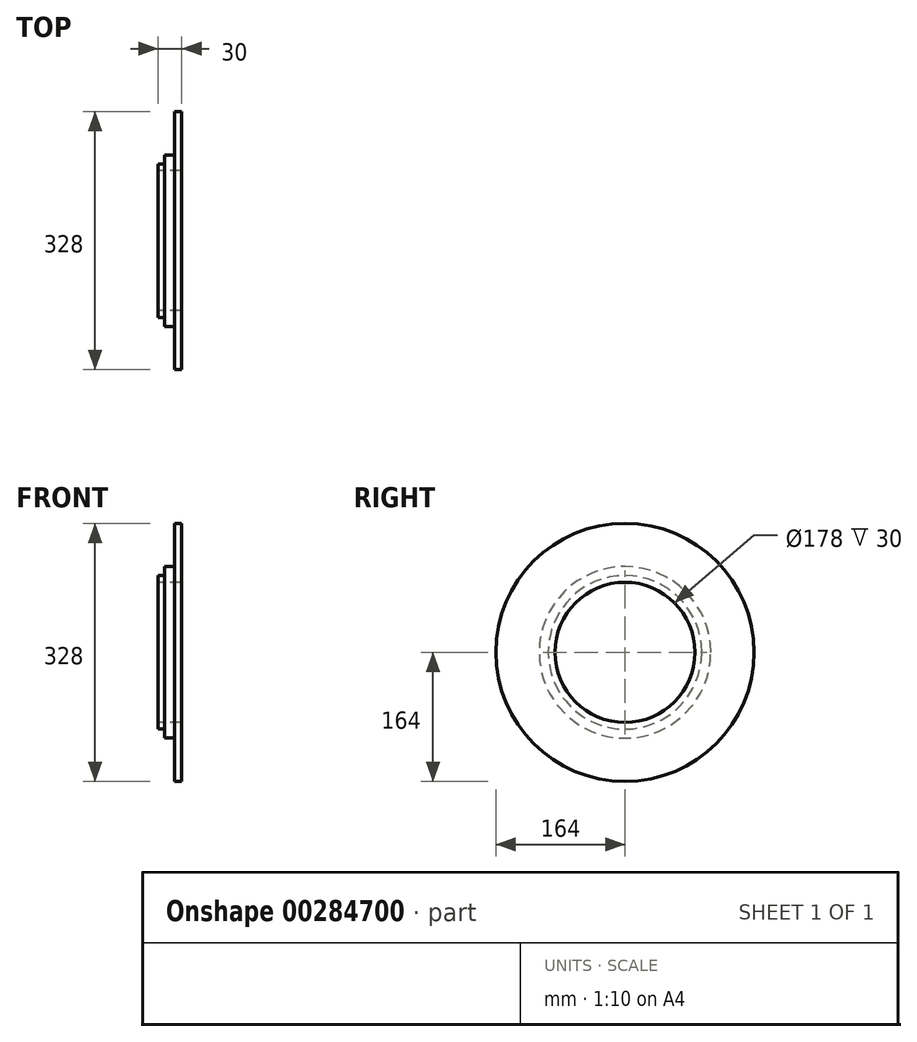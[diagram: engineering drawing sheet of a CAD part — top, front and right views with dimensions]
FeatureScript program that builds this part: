
annotation { "Feature Type Name" : "Feature", "Feature Type Description" : "" }
export const myFeature = defineFeature(function(context is Context, id is Id, definition is map)
    precondition{}
    {
        {
            var Q0;
            Q0=qCreatedBy(makeId("Front.planeOp"),FACE);
            var sketch = newSketch(context, id + "F0", { "sketchPlane" : qUnion([Q0])});
            skLineSegment(sketch, "E0", {"start": v(0, 89) * mm, "end": v(0, 164) * mm});
            skLineSegment(sketch, "E1", {"start": v(0, 164) * mm, "end": v(8, 164) * mm});
            skLineSegment(sketch, "E2", {"start": v(8, 164) * mm, "end": v(8, 89) * mm});
            skLineSegment(sketch, "E3", {"start": v(21, 89) * mm, "end": v(21, 164) * mm});
            skLineSegment(sketch, "E4", {"start": v(21, 164) * mm, "end": v(30, 164) * mm});
            skLineSegment(sketch, "E5", {"start": v(30, 164) * mm, "end": v(30, 89) * mm});
            skPoint(sketch, "E6", {"position": v(30, 97.5) * mm});
            skLineSegment(sketch, "E7", {"start": v(30, 97.5) * mm, "end": v(53.25, 97.5) * mm});
            skLineSegment(sketch, "E8", {"start": v(53.25, 97.5) * mm, "end": v(53.25, 0) * mm});
            skLineSegment(sketch, "E9", {"start": v(30, 89) * mm, "end": v(44.75, 89) * mm, "construction": true});
            skLineSegment(sketch, "E10", {"start": v(44.75, 89) * mm, "end": v(44.75, 0) * mm, "construction": true});
            skLineSegment(sketch, "E11", {"start": v(44.75, 0) * mm, "end": v(53.25, 0) * mm});
            skLineSegment(sketch, "E12", {"start": v(30, 97.5) * mm, "end": v(0, 97.5) * mm});
            skLineSegment(sketch, "E13", {"start": v(0, 97.5) * mm, "end": v(0, 89) * mm});
            skLineSegment(sketch, "E14", {"start": v(0, 89) * mm, "end": v(30, 89) * mm});
            skPoint(sketch, "E15", {"position": v(21, 109) * mm});
            skLineSegment(sketch, "E16", {"start": v(21, 109) * mm, "end": v(8, 109) * mm});
            skPoint(sketch, "E17", {"position": v(44.75, 60) * mm});
            skLineSegment(sketch, "E18", {"start": v(44.75, 60) * mm, "end": v(53.25, 60) * mm});
            skSolve(sketch);
        }
        {
            var Q0;
            {var subQ5=sQuery(id+"F0.wireOp",EDGE,"E0");Q0=makeQuery(id+"F0.imprint","IMPRINT",FACE,{"disambiguationData":[TD([[makeQuery(id+"F0.imprint","IMPRINT",EDGE,{"derivedFrom":subQ5}),-1.0]])]});}
            var Q1;
            {var subQ5=sQuery(id+"F0.wireOp",EDGE,"E13");Q1=makeQuery(id+"F0.imprint","IMPRINT",FACE,{"disambiguationData":[TD([[makeQuery(id+"F0.imprint","IMPRINT",EDGE,{"derivedFrom":subQ5}),1.0]])]});}
            var Q2;
            {var subQ1=sQuery(id+"F0.wireOp",EDGE,"E4");Q2=makeQuery(id+"F0.imprint","IMPRINT",FACE,{"disambiguationData":[TD([[makeQuery(id+"F0.imprint","IMPRINT",EDGE,{"derivedFrom":subQ1}),-1.0]])]});}
            var Q3;
            {var subQ2=sQuery(id+"F0.wireOp",EDGE,"E7");Q3=makeQuery(id+"F0.imprint","IMPRINT",FACE,{"disambiguationData":[TD([[makeQuery(id+"F0.imprint","IMPRINT",EDGE,{"derivedFrom":subQ2}),-1.0]])]});}
            var Q4;
            {var subQ0=sQuery(id+"F0.wireOp",EDGE,"E16");Q4=makeQuery(id+"F0.imprint","IMPRINT",FACE,{"disambiguationData":[TD([[makeQuery(id+"F0.imprint","IMPRINT",EDGE,{"derivedFrom":subQ0}),1.0]])]});}
            var Q5;
            {var subQ0=sQuery(id+"F0.wireOp",EDGE,"E14");var subQ1=sQuery(id+"F0.wireOp",EDGE,"E2");var subQ2=makeQuery(id+"F0.imprint","INTERSECT",VERTEX,{"derivedFrom":[subQ1,subQ0]});Q5=makeQuery(id+"F0.imprint","IMPRINT",FACE,{"disambiguationData":[TD([[makeQuery(id+"F0.imprint","IMPRINT",EDGE,{"disambiguationData":[TD([[subQ2,1.0]])],"derivedFrom":subQ1}),1.0]])]});}
            var Q6;
            {var subQ0=sQuery(id+"F0.wireOp",EDGE,"E14");var subQ1=sQuery(id+"F0.wireOp",EDGE,"E3");var subQ2=makeQuery(id+"F0.imprint","INTERSECT",VERTEX,{"derivedFrom":[subQ1,subQ0]});Q6=makeQuery(id+"F0.imprint","IMPRINT",FACE,{"disambiguationData":[TD([[makeQuery(id+"F0.imprint","IMPRINT",EDGE,{"disambiguationData":[TD([[subQ2,-1.0]])],"derivedFrom":subQ1}),-1.0]])]});}
            var Q7;
            Q7=sQuery(id+"F0.wireOp",EDGE,"E11");
            revolve(context, id + "F1", {"entities" : qUnion([Q0, Q1, Q2, Q3, Q4, Q5, Q6]), "axis" : qUnion([Q7]), "revolveType" : RevolveType.FULL});
        }
    });
